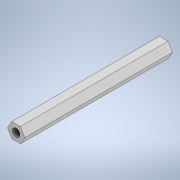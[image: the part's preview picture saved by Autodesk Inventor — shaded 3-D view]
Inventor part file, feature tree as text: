
AUTODESK INVENTOR PART (.ipt)
format: ipt  version: 2020 (Build 240168000, 168)  size: 111,104 bytes
history: native  units: in
note: dims shown in document units (in); Inventor stores cm internally (conversion verified against a paired STEP export)
features: sketch x2, extrude x1, hole x1, plane x1, mirror x1, projected_geometry x1
ambient origin geometry x8: Origin, YZ Plane, XZ Plane, XY Plane, X Axis, Y Axis, Z Axis, Center Point
bodies: Solid1 (feature_tree)
feature tree (7):
  extrude  "Extrusion1"  Depth=2.126in TaperAngle=0.0deg
  hole  "Hole1"  [1 undecoded]
  plane  "Work Plane1"
  mirror  "Mirror1"
  sketch  "Sketch1"  dims[d0=0.2165in d1=2.126in d2=0.0in]
  sketch  "Sketch2"  dims[d3=0.1122in d4=0.2756in d5=0.1575in d6=0.0787in d7=90.0deg d8=0.4094in d9=0.0in]
  projected_geometry  "Projected Loop1"
note: 1 required parameter value undecoded (feature->parameter linkage not recoverable at this tier; creation-order binding heuristic only, values carry confidence <= 0.55)
